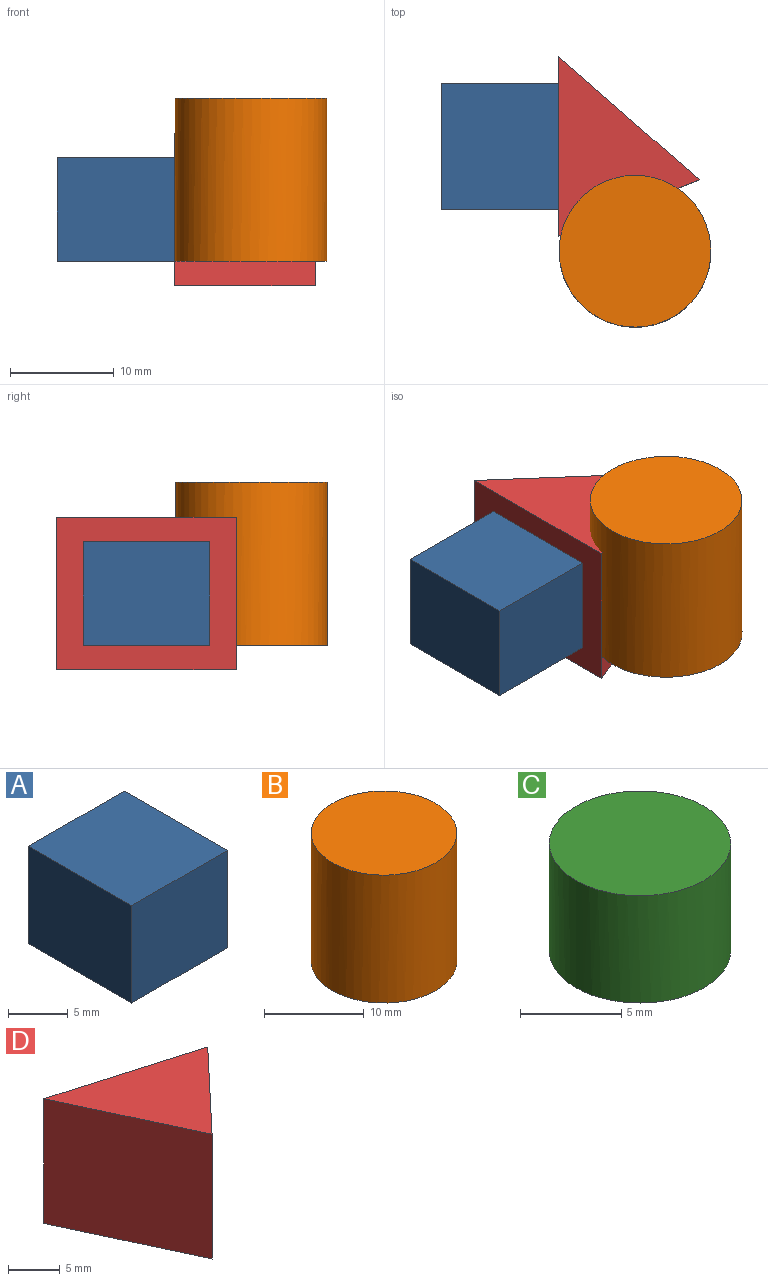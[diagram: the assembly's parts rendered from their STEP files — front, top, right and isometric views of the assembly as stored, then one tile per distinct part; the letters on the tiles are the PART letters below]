
ASSEMBLY  parts=4 mates=2
PART A: 6 faces, bbox 11.3x12.2x10 mm
  f0: plane 12.23x10mm, normal (-1,0,0), area 122.3mm2, adj f1,f2,f3,f4
  f1: plane 12.23x11.34mm, normal (0,0,-1), area 138.6mm2, adj f0,f2,f4,f5
  f2: plane 11.34x10mm, normal (0,1,0), area 113.4mm2, adj f0,f1,f3,f5
  f3: plane 12.23x11.34mm, normal (0,0,1), area 138.6mm2, adj f0,f2,f4,f5
  f4: plane 11.34x10mm, normal (0,-1,0), area 113.4mm2, adj f0,f1,f3,f5
  f5: plane 12.23x10mm, normal (1,0,0), area 122.3mm2, adj f1,f2,f3,f4
PART B: 3 faces, bbox 14.7x14.9x15.8 mm
  f0: plane 14.92x14.65mm, normal (0,0,1), area 168.6mm2, adj f2
  f1: plane 14.92x14.65mm, normal (0,0,-1), area 168.6mm2, adj f2
  f2: cylinder r=7.33mm len=15.75mm, axis (0,0,1), area 724.9mm2, adj f0,f1
PART C: 3 faces, bbox 9x9.1x6.5 mm
  f0: plane 9.15x8.98mm, normal (0,0,1), area 63.4mm2, adj f2
  f1: plane 9.15x8.98mm, normal (0,0,-1), area 63.4mm2, adj f2
  f2: cylinder r=4.49mm len=8.98mm, axis (0,0,1), area 183.4mm2, adj f0,f1
PART D: 5 faces, bbox 17.3x15.7x14.8 mm
  f0: plane 17.3x15.71mm, normal (0,0,-1), area 117.5mm2, adj f1,f3,f4
  f1: plane 15.71x14.75mm, normal (-0.91,-0.42,0), area 255.3mm2, adj f0,f2,f3,f4
  f2: plane 17.3x15.71mm, normal (0,0,1), area 117.5mm2, adj f1,f3,f4
  f3: plane 14.75x10.63mm, normal (0.73,-0.69,0), area 215.7mm2, adj f0,f1,f2,f4
  f4: plane 17.3x14.75mm, normal (0.28,0.96,0), area 266mm2, adj f0,f1,f2,f3
PLACE A at identity
PLACE B at identity
PLACE C t=(9.33,2.07,4.63)mm
PLACE D rot(axis=(0,0,-1),24.8deg) t=(-7.56,-0.71,-2.38)mm
MATE planar D.f1 <-> A.f5  axis (-1,0,0) through (-4.37,2.6,5)mm
MATE revolute C.f2 <-> B.f2  axis (0,0,1) through (3.01,-7.53,7.88)mm
